# Revit family: GMV-ND90-140PMSA1-T
name_source: partatom
category: 机械设备
revit_build: Autodesk Revit 2014 (Build: 20130308_1515(x64)
units: mm (PartAtom-declared; Revit-internal decimal feet)

## types (5) — shared parameters
air outlet height = 215  [stored 0.705381 ft]
drain pipe = 25  [stored 0.082021 ft]
gas pipe = 16
liquid pipe = 10  [stored 0.0328084 ft]
unit depth = 656
unit height = 260
unit width = 1340

## per-type parameters (varying)
| type | air outlet width | air return height | air return width | cooling capacity | heating capacity |
| GMV-ND90PMS/A1-T | 740 | 233 | 871 | 9000 W | 10000 W |
| GMV-ND100PMS/A1-T | 740 | 233 | 871 | 10000 W | 11200 W |
| GMV-ND112PMS/A1-T | 740 | 233 | 871 | 11200 W | 12500 W |
| GMV-ND125PMS/A1-T | 1155  [stored 3.78937 ft] | 220  [stored 0.721785 ft] | 1187  [stored 3.89436 ft] | 12500 W | 14000 W |
| GMV-ND140PMS/A1-T | 1155  [stored 3.78937 ft] | 220  [stored 0.721785 ft] | 1187  [stored 3.89436 ft] | 14000 W | 16000 W |

note: [stored X ft] marks values corroborated as IEEE doubles in the binary element streams (Revit-internal decimal feet)
